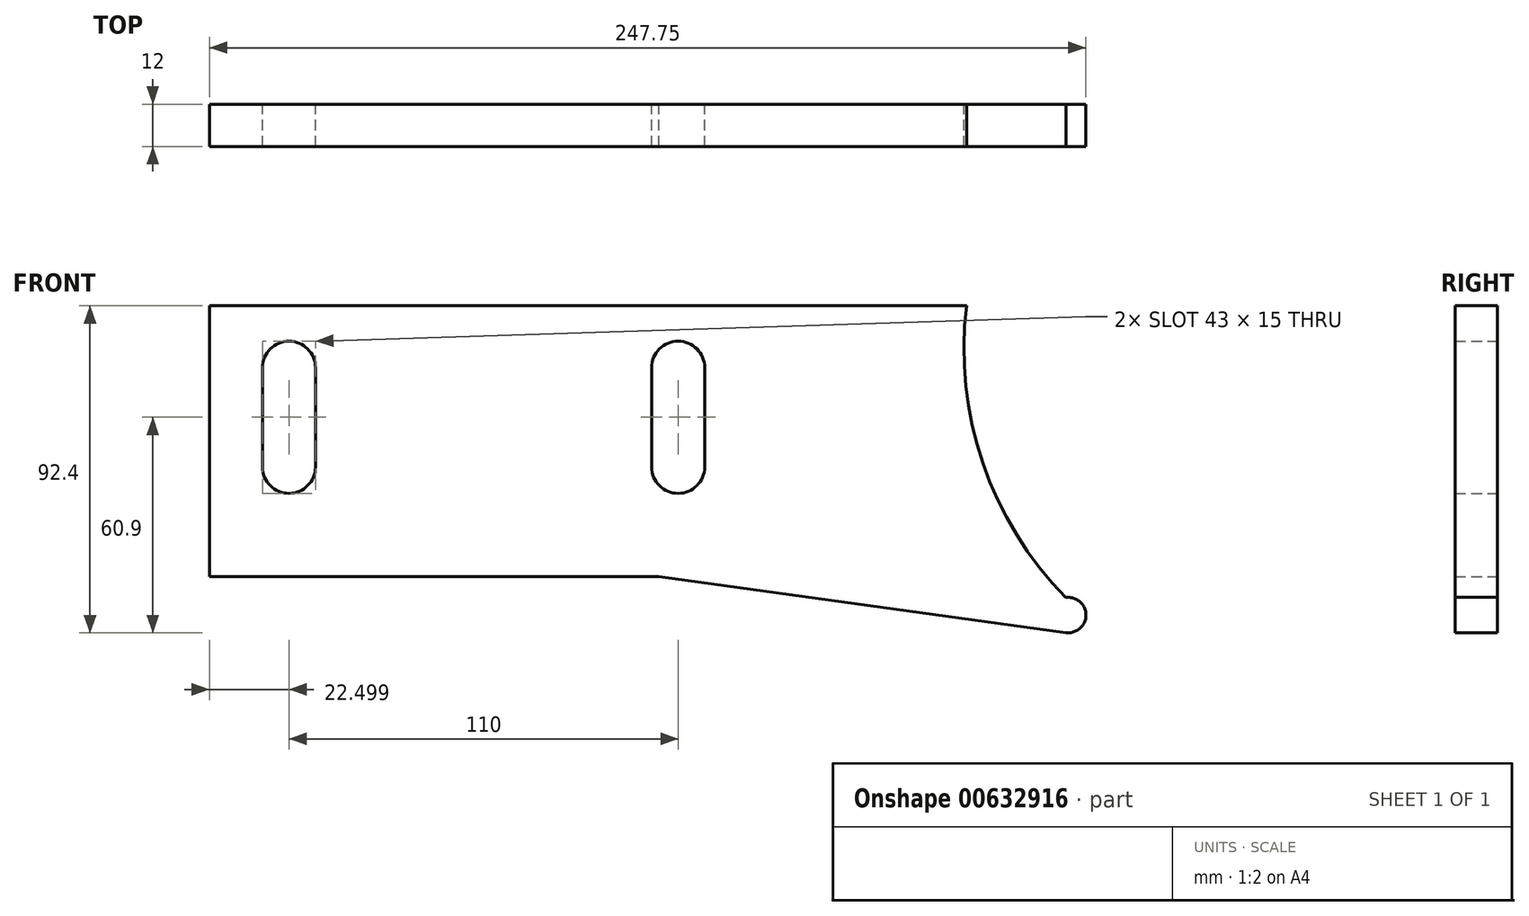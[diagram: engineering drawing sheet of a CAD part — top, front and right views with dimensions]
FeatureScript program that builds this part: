
annotation { "Feature Type Name" : "Feature", "Feature Type Description" : "" }
export const myFeature = defineFeature(function(context is Context, id is Id, definition is map)
    precondition{}
    {
        {
            var Q0;
            Q0=qCreatedBy(makeId("Front.planeOp"),FACE);
            var sketch = newSketch(context, id + "F0", { "sketchPlane" : qUnion([Q0])});
            skLineSegment(sketch, "E0", {"start": v(-78.35, -23.48) * mm, "end": v(-78.35, 52.52) * mm});
            skLineSegment(sketch, "E1", {"start": v(-78.35, 53) * mm, "end": v(129.92, 53) * mm});
            skPoint(sketch, "E2.end.orphan", {"position": v(-48.35, 21.5) * mm});
            skLineSegment(sketch, "E3", {"start": v(48.42, -0.19) * mm, "end": v(48.42, -0.37) * mm});
            skLineSegment(sketch, "E4", {"start": v(40.92, 0) * mm, "end": v(40.93, 0) * mm});
            skLineSegment(sketch, "E5", {"start": v(-78.35, 52.52) * mm, "end": v(-78.35, 53) * mm});
            skPoint(sketch, "E6.orphan", {"position": v(-84.08, 52.63) * mm});
            skLineSegment(sketch, "E7", {"start": v(129.92, 53) * mm, "end": v(135.65, 53) * mm});
            skLineSegment(sketch, "E8", {"start": v(-78.35, -23.48) * mm, "end": v(48.65, -23.48) * mm});
            skLineSegment(sketch, "E9", {"start": v(48.65, -23.48) * mm, "end": v(163.72, -39.35) * mm});
            skArc(sketch, "E10", {"start": v(135.65, 53) * mm, "mid": v(140.24, 8.56) * mm, "end": v(163.72, -29.45) * mm});
            skArc(sketch, "E11", {"start": v(163.72, -39.35) * mm, "mid": v(169.4, -34.4) * mm, "end": v(163.72, -29.45) * mm});
            skLineSegment(sketch, "E12", {"start": v(-78.35, 53) * mm, "end": v(-55.85, 53) * mm});
            skLineSegment(sketch, "E13", {"start": v(-63.35, 21.5) * mm, "end": v(-63.35, 35.5) * mm});
            skLineSegment(sketch, "E14", {"start": v(-48.35, 35.5) * mm, "end": v(-48.35, 7.5) * mm});
            skLineSegment(sketch, "E15", {"start": v(-63.35, 7.5) * mm, "end": v(-63.35, 21.5) * mm});
            skArc(sketch, "E16", {"start": v(-48.35, 35.5) * mm, "mid": v(-55.85, 43) * mm, "end": v(-63.35, 35.5) * mm});
            skArc(sketch, "E17.MirrorC", {"start": v(-48.35, 7.5) * mm, "mid": v(-55.85, 0) * mm, "end": v(-63.35, 7.5) * mm});
            skPoint(sketch, "E18.start.orphan", {"position": v(-55.85, 43) * mm});
            skPoint(sketch, "E19.orphan", {"position": v(-48.35, 43) * mm});
            skPoint(sketch, "E20.orphan", {"position": v(-63.35, 43) * mm});
            skPoint(sketch, "E21.orphan", {"position": v(-48.35, 0) * mm});
            skPoint(sketch, "E22.end.orphan", {"position": v(-63.35, 0) * mm});
            skLineSegment(sketch, "E23", {"start": v(46.65, 21.5) * mm, "end": v(46.65, 35.5) * mm});
            skLineSegment(sketch, "E24", {"start": v(61.65, 35.5) * mm, "end": v(61.65, 7.5) * mm});
            skLineSegment(sketch, "E25", {"start": v(46.65, 7.5) * mm, "end": v(46.65, 21.5) * mm});
            skArc(sketch, "E26", {"start": v(61.65, 35.5) * mm, "mid": v(54.15, 43) * mm, "end": v(46.65, 35.5) * mm});
            skArc(sketch, "E27.MirrorC", {"start": v(61.65, 7.5) * mm, "mid": v(54.15, 0) * mm, "end": v(46.65, 7.5) * mm});
            skPoint(sketch, "E28.end.orphan", {"position": v(61.65, 43) * mm});
            skPoint(sketch, "E29.end.orphan", {"position": v(46.65, -0.19) * mm});
            skPoint(sketch, "E30.orphan", {"position": v(61.65, 0) * mm});
            skPoint(sketch, "E31.start.orphan", {"position": v(-55.85, 21.5) * mm});
            skPoint(sketch, "E32.start.orphan", {"position": v(54.15, 21.5) * mm});
            skPoint(sketch, "E33.start.orphan", {"position": v(54.15, 43) * mm});
            skPoint(sketch, "E34.trimOffspring.end.orphan", {"position": v(-55.85, 0) * mm});
            skSolve(sketch);
        }
        {
            var Q0;
            Q0=makeQuery(id+"F0.imprint","IMPRINT",FACE,{"disambiguationData":[TD([[makeQuery(id+"F0.imprint","IMPRINT",EDGE,{"derivedFrom":sQuery(id+"F0.wireOp",EDGE,"2O0Lhi2r-tiX1-HgMG-9HXu-j3PjuiEXZLxa")}),1.0]])]});
            var Q1;
            Q1=makeQuery(id+"F0.imprint","IMPRINT",FACE,{"disambiguationData":[TD([[makeQuery(id+"F0.imprint","IMPRINT",EDGE,{"derivedFrom":sQuery(id+"F0.wireOp",EDGE,"E0")}),-1.0]])]});
            extrude(context, id + "F1", {"entities" : qUnion([Q0, Q1]), "depth" : 12 * mm, "offsetDistance" : 25 * mm});
        }
    });
